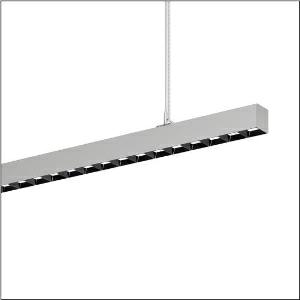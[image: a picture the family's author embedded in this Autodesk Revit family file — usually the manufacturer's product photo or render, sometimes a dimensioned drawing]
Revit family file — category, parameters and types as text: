
# Revit family: silica_r__21_51mx32dc3dsb_c9e6
name_source: partatom
category: Lighting Fixtures
units: mm (PartAtom-declared; Revit-internal decimal feet)

## family parameters
Cut with Voids When Loaded = No
Host = Face
Light Source = No
Part Type = Normal
Room Calculation Point = No
Round Connector Dimension = Use Diameter
Shared = No

## types (1)
- --- (1 x LED, 18220 lm, 113 W, 3000K)
    Apparent Load = 113 VA
    CIE Flux Codes = 86 99 100 59 100
    Color Rendering = 80
    Color Temperature = 3000K
    Default Elevation = 1800 mm
    Description = Silica® 21, office luminaire, primary light control with darklight reflector, of PMMA, black, CAT 2 (L<= 3000cd/m²), light emission: direct/indirect distribution, primary light characteristic: symmetric, installation type: suspended mounting, LED, rated luminous flux: 18.220lm, luminous efficacy: 161lm/W, light colour: 830, colour temperature: 3000K, with terminal, 3+2-pole, max. 2.5mm², mains connection: 220..240V, AC, 50/60Hz, rated input power: 113W, luminaire housing, of aluminium, metallic grey (RAL 9006), length: 3.004mm, width: 53mm, height: 53mm, protection rating (complete): IP20, insulation class (complete): insulation class I (protective earthing), certification: CE, permissible operating ambient temperature: 0..+35°C, standard: EN 50419, packaging unit: 1 piece
    Height = 53 mm
    Lamp = 1 x LED
    Lamp Light Flux = 18220 lm
    Lamp Power = 113 W
    Lamp count = 1
    Length = 3004 mm
    Luminous efficacy = 161 lm/W
    Manufacturer = Siteco
    ModVariant = No
    Model = 51MX32DC3DSB
    Mounting Place = Ceiling
    Mounting Type = Pendant
    Number of Poles = 1
    OnlyDefault = Yes
    Power Factor = 1
    Product Name = Silica® 21
    Product group = office luminaire | ceiling pendant
    ProductGroupID = 902
    Protection Class = Protection class I
    Protection Degree = IP 20
    RLX_Detail_Level = 1
    RLX_Emergency_Light_Flux = 0 lm
    RLX_Emergency_Type = 0
    RLX_Emergency_Type_DB = No
    RlxData = <blob elided: 65301 chars, md5=f28ac6ae>
    Socket = socket
    Standby Power = 0 W
    System Light Flux = 18220 lm
    System Power = 113 W
    Type Comments = factory setting: luminous flux: 100 % | dim-lin: 254 | 391 mA
    Type Image = l_1313642.jpg
    URL = http://relux.com
    VarID = @adj_070795
    Voltage = 0 V
    Weight = 0.00 kg
    Width = 53 mm

## geometry (parser evidence)
native form markers: Blend x4, Sweep x14
no freeform markers — native parametric forms only
